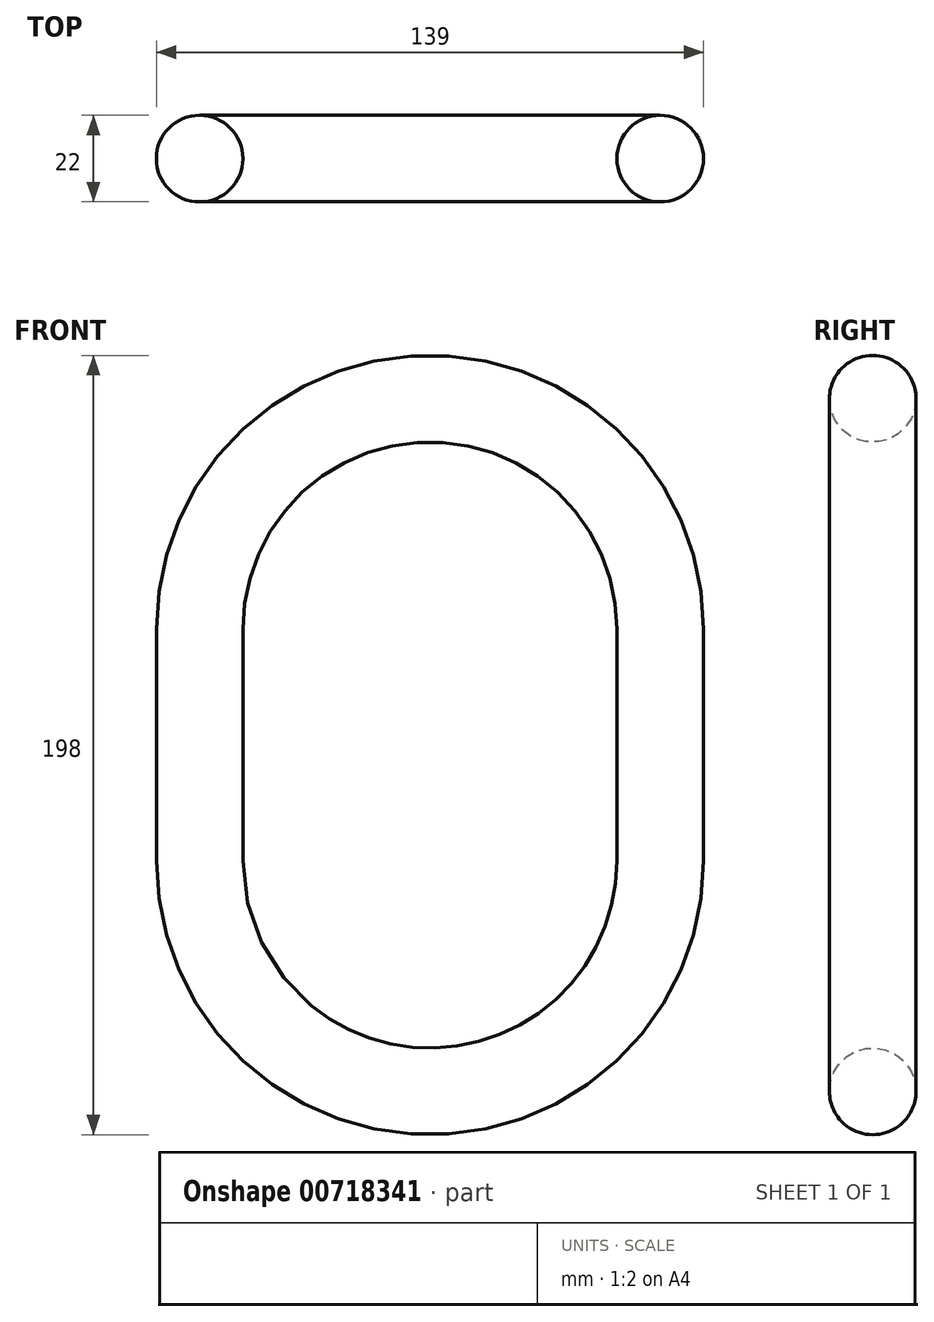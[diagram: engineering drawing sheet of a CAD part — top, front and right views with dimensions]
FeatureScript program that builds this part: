
annotation { "Feature Type Name" : "Feature", "Feature Type Description" : "" }
export const myFeature = defineFeature(function(context is Context, id is Id, definition is map)
    precondition{}
    {
        {
            var Q0;
            Q0=qCreatedBy(makeId("Top.planeOp"),FACE);
            var sketch = newSketch(context, id + "F0", { "sketchPlane" : qUnion([Q0])});
            skLineSegment(sketch, "E0", {"start": v(0, 0) * mm, "end": v(58.5, 0) * mm, "construction": true});
            skCircle(sketch, "E1", {"center": v(58.5, 0) * mm, "radius": 11 * mm});
            skSolve(sketch);
        }
        {
            var Q0;
            Q0=qCreatedBy(makeId("Front.planeOp"),FACE);
            var sketch = newSketch(context, id + "F1", { "sketchPlane" : qUnion([Q0])});
            skLineSegment(sketch, "E2", {"start": v(0, 0) * mm, "end": v(0, 77) * mm, "construction": true});
            skArc(sketch, "E3", {"start": v(47.5, 29.5) * mm, "mid": v(0, 77) * mm, "end": v(-47.5, 29.5) * mm});
            skLineSegment(sketch, "E4", {"start": v(47.5, 29.5) * mm, "end": v(47.5, 0) * mm});
            skLineSegment(sketch, "E5.MirrorCS", {"start": v(-47.5, 29.5) * mm, "end": v(-47.5, 0) * mm});
            skLineSegment(sketch, "E6.MirrorCS", {"start": v(47.5, -29.5) * mm, "end": v(47.5, 0) * mm});
            skLineSegment(sketch, "E7.MirrorCS", {"start": v(-47.5, -29.5) * mm, "end": v(-47.5, 0) * mm});
            skArc(sketch, "E8.MirrorC", {"start": v(47.5, -29.5) * mm, "mid": v(0, -77) * mm, "end": v(-47.5, -29.5) * mm});
            skSolve(sketch);
        }
        {
            var Q0;
            Q0=makeQuery(id+"F0.imprint","IMPRINT",FACE,{"disambiguationData":[TD([[makeQuery(id+"F0.imprint","IMPRINT",EDGE,{"derivedFrom":sQuery(id+"F0.wireOp",EDGE,"E1")}),1.0]])]});
            var Q1;
            Q1=sQuery(id+"F1.wireOp",EDGE,"E4");
            var Q2;
            Q2=sQuery(id+"F1.wireOp",EDGE,"E3");
            var Q3;
            Q3=sQuery(id+"F1.wireOp",EDGE,"E5.MirrorCS");
            var Q4;
            Q4=sQuery(id+"F1.wireOp",EDGE,"E7.MirrorCS");
            var Q5;
            Q5=sQuery(id+"F1.wireOp",EDGE,"E8.MirrorC");
            var Q6;
            Q6=sQuery(id+"F1.wireOp",EDGE,"E6.MirrorCS");
            sweep(context, id + "F2", {"profiles" : qUnion([Q0]), "path" : qUnion([Q1, Q2, Q3, Q4, Q5, Q6])});
        }
    });
